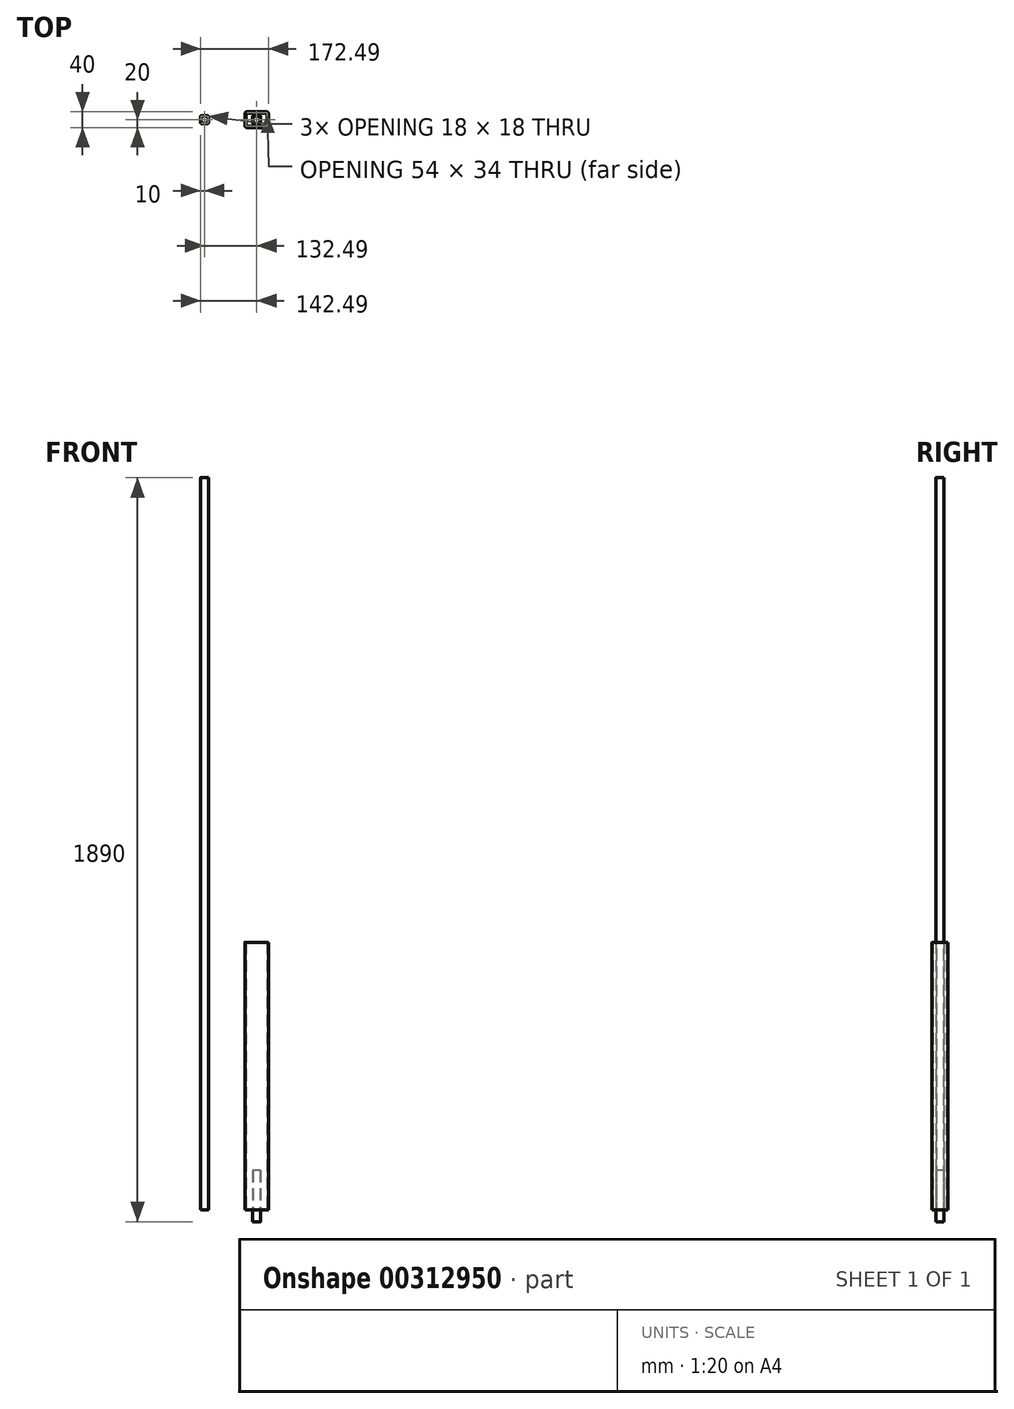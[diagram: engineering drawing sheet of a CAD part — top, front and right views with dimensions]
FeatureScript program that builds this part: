
annotation { "Feature Type Name" : "Feature", "Feature Type Description" : "" }
export const myFeature = defineFeature(function(context is Context, id is Id, definition is map)
    precondition{}
    {
        {
            var Q0;
            Q0=qCreatedBy(makeId("Top.planeOp"),FACE);
            var sketch = newSketch(context, id + "F0", { "sketchPlane" : qUnion([Q0])});
            skLineSegment(sketch, "E0.bottom", {"start": v(25, 20) * mm, "end": v(-25, 20) * mm});
            skLineSegment(sketch, "E0.top", {"start": v(25, -20) * mm, "end": v(-25, -20) * mm});
            skLineSegment(sketch, "E0.left", {"start": v(30, 15) * mm, "end": v(30, -15) * mm});
            skLineSegment(sketch, "E0.right", {"start": v(-30, 15) * mm, "end": v(-30, -15) * mm});
            skPoint(sketch, "E0.middle", {"position": v(0, 0) * mm});
            skLineSegment(sketch, "E1.0", {"start": v(25, 17) * mm, "end": v(-25, 17) * mm});
            skLineSegment(sketch, "E2.0", {"start": v(27, 15) * mm, "end": v(27, -15) * mm});
            skLineSegment(sketch, "E3.0", {"start": v(25, -17) * mm, "end": v(-25, -17) * mm});
            skLineSegment(sketch, "E4.0", {"start": v(-27, 15) * mm, "end": v(-27, -15) * mm});
            skPoint(sketch, "E5.visualSharp", {"position": v(-30, 20) * mm});
            skArc(sketch, "E5.filletArc", {"start": v(-25, 20) * mm, "mid": v(-28.54, 18.54) * mm, "end": v(-30, 15) * mm});
            skPoint(sketch, "E6.visualSharp", {"position": v(30, 20) * mm});
            skArc(sketch, "E6.filletArc", {"start": v(30, 15) * mm, "mid": v(28.54, 18.54) * mm, "end": v(25, 20) * mm});
            skPoint(sketch, "E7.visualSharp", {"position": v(30, -20) * mm});
            skArc(sketch, "E7.filletArc", {"start": v(25, -20) * mm, "mid": v(28.54, -18.54) * mm, "end": v(30, -15) * mm});
            skPoint(sketch, "E8.visualSharp", {"position": v(-30, -20) * mm});
            skArc(sketch, "E8.filletArc", {"start": v(-30, -15) * mm, "mid": v(-28.54, -18.54) * mm, "end": v(-25, -20) * mm});
            skPoint(sketch, "E9.visualSharp", {"position": v(-27, 17) * mm});
            skArc(sketch, "E9.filletArc", {"start": v(-25, 17) * mm, "mid": v(-26.41, 16.41) * mm, "end": v(-27, 15) * mm});
            skPoint(sketch, "E10.visualSharp", {"position": v(27, 17) * mm});
            skArc(sketch, "E10.filletArc", {"start": v(27, 15) * mm, "mid": v(26.41, 16.41) * mm, "end": v(25, 17) * mm});
            skPoint(sketch, "E11.visualSharp", {"position": v(27, -17) * mm});
            skArc(sketch, "E11.filletArc", {"start": v(25, -17) * mm, "mid": v(26.41, -16.41) * mm, "end": v(27, -15) * mm});
            skPoint(sketch, "E12.visualSharp", {"position": v(-27, -17) * mm});
            skArc(sketch, "E12.filletArc", {"start": v(-27, -15) * mm, "mid": v(-26.41, -16.41) * mm, "end": v(-25, -17) * mm});
            skSolve(sketch);
        }
        {
            var Q0;
            Q0 = qSketchRegion(id + "F0", true);
            extrude(context, id + "F1", {"entities" : qUnion([Q0]), "depth" : 680 * mm});
        }
        {
            var Q0;
            Q0=qCreatedBy(makeId("Top.planeOp"),FACE);
            var sketch = newSketch(context, id + "F2", { "sketchPlane" : qUnion([Q0])});
            skLineSegment(sketch, "E13.bottom", {"start": v(-124.5, 10) * mm, "end": v(-140.5, 10) * mm});
            skLineSegment(sketch, "E13.top", {"start": v(-124.5, -10) * mm, "end": v(-140.5, -10) * mm});
            skLineSegment(sketch, "E13.left", {"start": v(-122.5, 8) * mm, "end": v(-122.5, -8) * mm});
            skLineSegment(sketch, "E13.right", {"start": v(-142.5, 8) * mm, "end": v(-142.5, -8) * mm});
            skPoint(sketch, "E13.middle", {"position": v(-132.5, 0) * mm});
            skLineSegment(sketch, "E14.0", {"start": v(-124.5, 9) * mm, "end": v(-140.5, 9) * mm});
            skLineSegment(sketch, "E14.1", {"start": v(-123.5, 8) * mm, "end": v(-123.5, -8) * mm});
            skLineSegment(sketch, "E15.0", {"start": v(-124.5, -9) * mm, "end": v(-140.5, -9) * mm});
            skLineSegment(sketch, "E16.0", {"start": v(-141.5, 8) * mm, "end": v(-141.5, -8) * mm});
            skPoint(sketch, "E17.visualSharp", {"position": v(-141.5, 9) * mm});
            skArc(sketch, "E17.filletArc", {"start": v(-140.5, 9) * mm, "mid": v(-141.2, 8.7) * mm, "end": v(-141.5, 8) * mm});
            skPoint(sketch, "E18.visualSharp", {"position": v(-123.5, 9) * mm});
            skArc(sketch, "E18.filletArc", {"start": v(-123.5, 8) * mm, "mid": v(-123.78, 8.7) * mm, "end": v(-124.5, 9) * mm});
            skPoint(sketch, "E19.visualSharp", {"position": v(-123.5, -9) * mm});
            skArc(sketch, "E19.filletArc", {"start": v(-124.5, -9) * mm, "mid": v(-123.78, -8.7) * mm, "end": v(-123.5, -8) * mm});
            skPoint(sketch, "E20.visualSharp", {"position": v(-141.5, -9) * mm});
            skArc(sketch, "E20.filletArc", {"start": v(-141.5, -8) * mm, "mid": v(-141.2, -8.7) * mm, "end": v(-140.5, -9) * mm});
            skPoint(sketch, "E21.visualSharp", {"position": v(-142.5, 10) * mm});
            skArc(sketch, "E21.filletArc", {"start": v(-140.5, 10) * mm, "mid": v(-141.9, 9.41) * mm, "end": v(-142.5, 8) * mm});
            skPoint(sketch, "E22.visualSharp", {"position": v(-122.5, 10) * mm});
            skArc(sketch, "E22.filletArc", {"start": v(-122.5, 8) * mm, "mid": v(-123.08, 9.41) * mm, "end": v(-124.5, 10) * mm});
            skPoint(sketch, "E23.visualSharp", {"position": v(-122.5, -10) * mm});
            skArc(sketch, "E23.filletArc", {"start": v(-124.5, -10) * mm, "mid": v(-123.08, -9.41) * mm, "end": v(-122.5, -8) * mm});
            skPoint(sketch, "E24.visualSharp", {"position": v(-142.5, -10) * mm});
            skArc(sketch, "E24.filletArc", {"start": v(-142.5, -8) * mm, "mid": v(-141.9, -9.41) * mm, "end": v(-140.5, -10) * mm});
            skSolve(sketch);
        }
        {
            var Q0;
            Q0 = qSketchRegion(id + "F2", true);
            extrude(context, id + "F3", {"entities" : qUnion([Q0]), "depth" : 1860 * mm, "offsetDistance" : 25 * mm});
        }
        {
            var Q0;
            Q0=qCreatedBy(makeId("Top.planeOp"),FACE);
            var sketch = newSketch(context, id + "F4", { "sketchPlane" : qUnion([Q0])});
            skLineSegment(sketch, "E25.bottom", {"start": v(8, 10) * mm, "end": v(-8, 10) * mm});
            skLineSegment(sketch, "E25.top", {"start": v(8, -10) * mm, "end": v(-8, -10) * mm});
            skLineSegment(sketch, "E25.left", {"start": v(10, 8) * mm, "end": v(10, -8) * mm});
            skLineSegment(sketch, "E25.right", {"start": v(-10, 8) * mm, "end": v(-10, -8) * mm});
            skPoint(sketch, "E25.middle", {"position": v(0, 0) * mm});
            skLineSegment(sketch, "E26.0", {"start": v(8, 9) * mm, "end": v(-8, 9) * mm});
            skLineSegment(sketch, "E26.1", {"start": v(9, 8) * mm, "end": v(9, -8) * mm});
            skLineSegment(sketch, "E27.0", {"start": v(8, -9) * mm, "end": v(-8, -9) * mm});
            skLineSegment(sketch, "E28.0", {"start": v(-9, 8) * mm, "end": v(-9, -8) * mm});
            skPoint(sketch, "E29.visualSharp", {"position": v(-9, 9) * mm});
            skArc(sketch, "E29.filletArc", {"start": v(-8, 9) * mm, "mid": v(-8.7, 8.7) * mm, "end": v(-9, 8) * mm});
            skPoint(sketch, "E30.visualSharp", {"position": v(9, 9) * mm});
            skArc(sketch, "E30.filletArc", {"start": v(9, 8) * mm, "mid": v(8.7, 8.7) * mm, "end": v(8, 9) * mm});
            skPoint(sketch, "E31.visualSharp", {"position": v(9, -9) * mm});
            skArc(sketch, "E31.filletArc", {"start": v(8, -9) * mm, "mid": v(8.7, -8.7) * mm, "end": v(9, -8) * mm});
            skPoint(sketch, "E32.visualSharp", {"position": v(-9, -9) * mm});
            skArc(sketch, "E32.filletArc", {"start": v(-9, -8) * mm, "mid": v(-8.7, -8.7) * mm, "end": v(-8, -9) * mm});
            skPoint(sketch, "E33.visualSharp", {"position": v(-10, 10) * mm});
            skArc(sketch, "E33.filletArc", {"start": v(-8, 10) * mm, "mid": v(-9.41, 9.41) * mm, "end": v(-10, 8) * mm});
            skPoint(sketch, "E34.visualSharp", {"position": v(10, 10) * mm});
            skArc(sketch, "E34.filletArc", {"start": v(10, 8) * mm, "mid": v(9.41, 9.41) * mm, "end": v(8, 10) * mm});
            skPoint(sketch, "E35.visualSharp", {"position": v(10, -10) * mm});
            skArc(sketch, "E35.filletArc", {"start": v(8, -10) * mm, "mid": v(9.41, -9.41) * mm, "end": v(10, -8) * mm});
            skPoint(sketch, "E36.visualSharp", {"position": v(-10, -10) * mm});
            skArc(sketch, "E36.filletArc", {"start": v(-10, -8) * mm, "mid": v(-9.41, -9.41) * mm, "end": v(-8, -10) * mm});
            skSolve(sketch);
        }
        {
            var Q0;
            Q0=makeQuery(id+"F4.imprint","IMPRINT",FACE,{"disambiguationData":[TD([[makeQuery(id+"F4.imprint","IMPRINT",EDGE,{"derivedFrom":sQuery(id+"F4.wireOp",EDGE,"E25.bottom")}),1.0]])]});
            extrude(context, id + "F5", {"entities" : qUnion([Q0]), "depth" : 100 * mm, "offsetDistance" : 25 * mm});
        }
        {
            var Q0;
            Q0=qCreatedBy(makeId("Top.planeOp"),FACE);
            var sketch = newSketch(context, id + "F6", { "sketchPlane" : qUnion([Q0])});
            skLineSegment(sketch, "E37.0.0", {"start": v(8, -10) * mm, "end": v(-8, -10) * mm});
            skArc(sketch, "E37.0.1", {"start": v(-8, -10) * mm, "mid": v(-9.41, -9.41) * mm, "end": v(-10, -8) * mm});
            skLineSegment(sketch, "E37.0.2", {"start": v(-10, -8) * mm, "end": v(-10, 8) * mm});
            skArc(sketch, "E37.0.3", {"start": v(-10, 8) * mm, "mid": v(-9.41, 9.41) * mm, "end": v(-8, 10) * mm});
            skLineSegment(sketch, "E37.0.4", {"start": v(-8, 10) * mm, "end": v(8, 10) * mm});
            skArc(sketch, "E37.0.5", {"start": v(8, 10) * mm, "mid": v(9.41, 9.41) * mm, "end": v(10, 8) * mm});
            skLineSegment(sketch, "E37.0.6", {"start": v(10, 8) * mm, "end": v(10, -8) * mm});
            skArc(sketch, "E37.0.7", {"start": v(10, -8) * mm, "mid": v(9.41, -9.41) * mm, "end": v(8, -10) * mm});
            skLineSegment(sketch, "E38.0", {"start": v(-9, 8) * mm, "end": v(-9, -8) * mm});
            skArc(sketch, "E39.0", {"start": v(-9, -8) * mm, "mid": v(-8.7, -8.7) * mm, "end": v(-8, -9) * mm});
            skLineSegment(sketch, "E40.0", {"start": v(8, -9) * mm, "end": v(-8, -9) * mm});
            skPoint(sketch, "E41.0", {"position": v(8.7, -8.7) * mm});
            skLineSegment(sketch, "E42.0", {"start": v(9, 8) * mm, "end": v(9, -8) * mm});
            skPoint(sketch, "E43.0", {"position": v(8.7, 8.7) * mm});
            skLineSegment(sketch, "E44.0", {"start": v(8, 9) * mm, "end": v(-8, 9) * mm});
            skArc(sketch, "E45.0", {"start": v(-8, 9) * mm, "mid": v(-8.7, 8.7) * mm, "end": v(-9, 8) * mm});
            skArc(sketch, "E46.0", {"start": v(9, 8) * mm, "mid": v(8.7, 8.7) * mm, "end": v(8, 9) * mm});
            skArc(sketch, "E47.0", {"start": v(8, -9) * mm, "mid": v(8.7, -8.7) * mm, "end": v(9, -8) * mm});
            skSolve(sketch);
        }
        {
            var Q0;
            Q0 = qSketchRegion(id + "F6", true);
            extrude(context, id + "F7", {"entities" : qUnion([Q0]), "depth" : -30 * mm, "offsetDistance" : 25 * mm});
        }
    });
